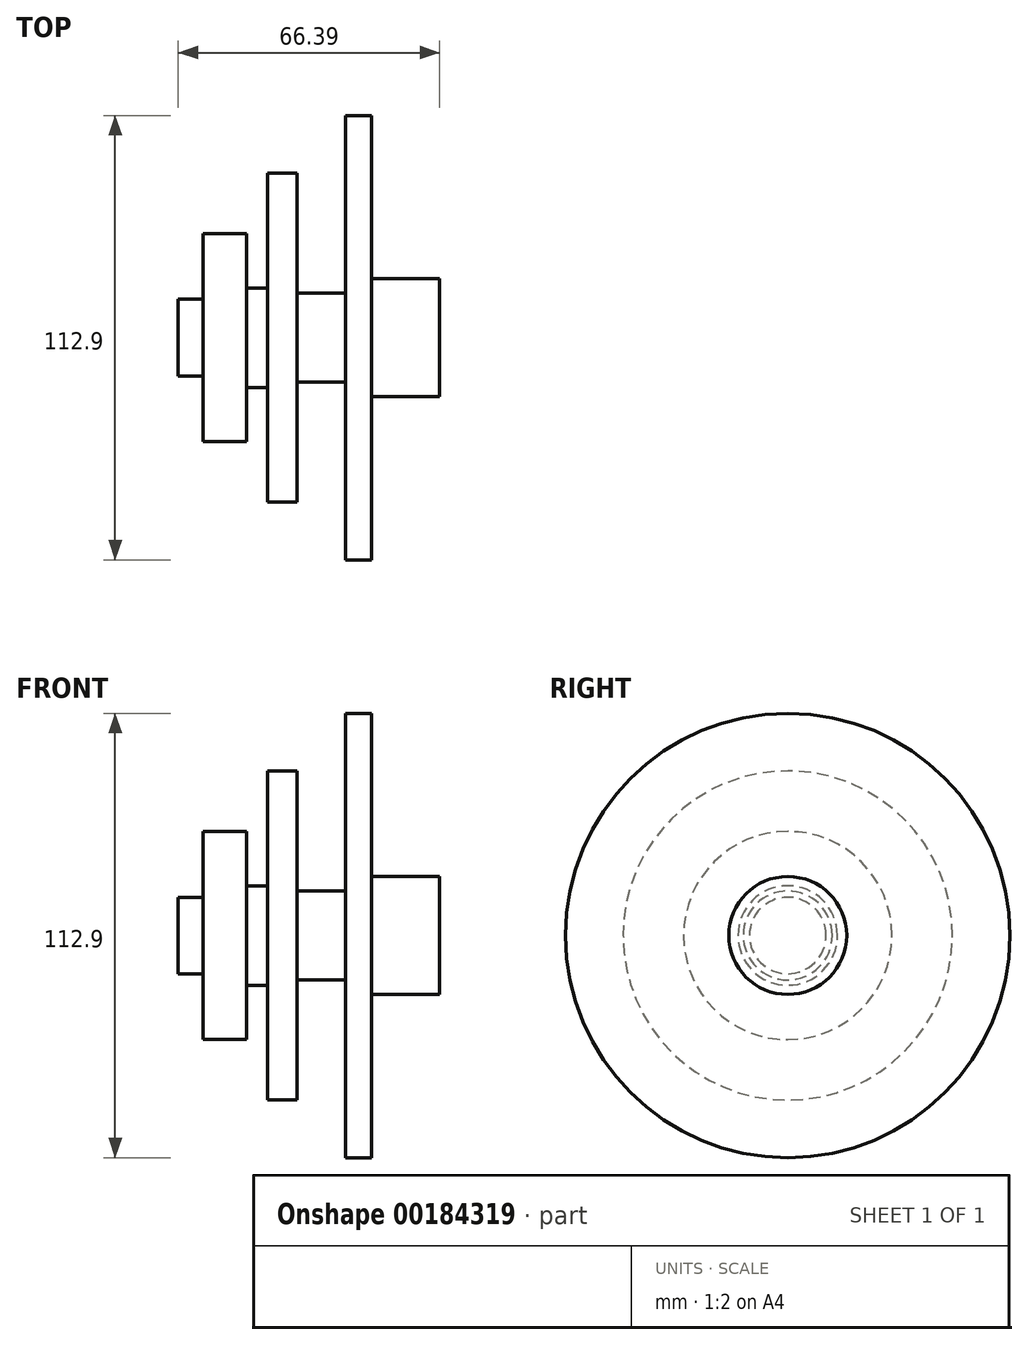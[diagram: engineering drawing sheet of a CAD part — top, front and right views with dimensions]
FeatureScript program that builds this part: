
annotation { "Feature Type Name" : "Feature", "Feature Type Description" : "" }
export const myFeature = defineFeature(function(context is Context, id is Id, definition is map)
    precondition{}
    {
        {
            var Q0;
            Q0=qCreatedBy(makeId("Front.planeOp"),FACE);
            var sketch = newSketch(context, id + "F0", { "sketchPlane" : qUnion([Q0])});
            skLineSegment(sketch, "E0", {"start": v(36.18, 0) * mm, "end": v(36.18, 14.98) * mm});
            skLineSegment(sketch, "E1", {"start": v(36.18, 14.98) * mm, "end": v(18.92, 14.98) * mm});
            skLineSegment(sketch, "E2", {"start": v(18.92, 14.98) * mm, "end": v(18.92, 25.73) * mm});
            skLineSegment(sketch, "E3", {"start": v(18.92, 25.73) * mm, "end": v(18.92, 56.45) * mm});
            skLineSegment(sketch, "E4", {"start": v(18.92, 56.45) * mm, "end": v(12.26, 56.45) * mm});
            skLineSegment(sketch, "E5", {"start": v(12.26, 56.45) * mm, "end": v(12.26, 11.3) * mm});
            skLineSegment(sketch, "E6", {"start": v(12.26, 11.3) * mm, "end": v(0, 11.3) * mm});
            skLineSegment(sketch, "E7", {"start": v(0, 11.3) * mm, "end": v(0, 41.81) * mm});
            skLineSegment(sketch, "E8", {"start": v(0, 41.81) * mm, "end": v(-7.5, 41.81) * mm});
            skLineSegment(sketch, "E9", {"start": v(-7.5, 41.81) * mm, "end": v(-7.5, 12.63) * mm});
            skLineSegment(sketch, "E10", {"start": v(-7.5, 12.63) * mm, "end": v(-12.8, 12.63) * mm});
            skLineSegment(sketch, "E11", {"start": v(-12.8, 12.63) * mm, "end": v(-12.8, 26.45) * mm});
            skLineSegment(sketch, "E12", {"start": v(-12.8, 26.45) * mm, "end": v(-23.9, 26.45) * mm});
            skLineSegment(sketch, "E13", {"start": v(-23.9, 26.45) * mm, "end": v(-23.9, 9.73) * mm});
            skLineSegment(sketch, "E14", {"start": v(-23.9, 9.73) * mm, "end": v(-30.2, 9.73) * mm});
            skLineSegment(sketch, "E15", {"start": v(-30.2, 9.73) * mm, "end": v(-30.2, 0) * mm});
            skLineSegment(sketch, "E16", {"start": v(-30.2, 0) * mm, "end": v(36.18, 0) * mm});
            skSolve(sketch);
        }
        {
            var Q0;
            Q0=qCreatedBy(makeId("Front.planeOp"),FACE);
            var sketch = newSketch(context, id + "F1", { "sketchPlane" : qUnion([Q0])});
            skLineSegment(sketch, "E17", {"start": v(-91.99, 0) * mm, "end": v(136.2, 0) * mm, "construction": true});
            skSolve(sketch);
        }
        {
            var Q0;
            Q0 = qSketchRegion(id + "F0", true);
            var Q1;
            Q1=sQuery(id+"F1.wireOp",EDGE,"E17");
            revolve(context, id + "F2", {"entities" : qUnion([Q0]), "axis" : qUnion([Q1]), "revolveType" : RevolveType.FULL});
        }
    });
